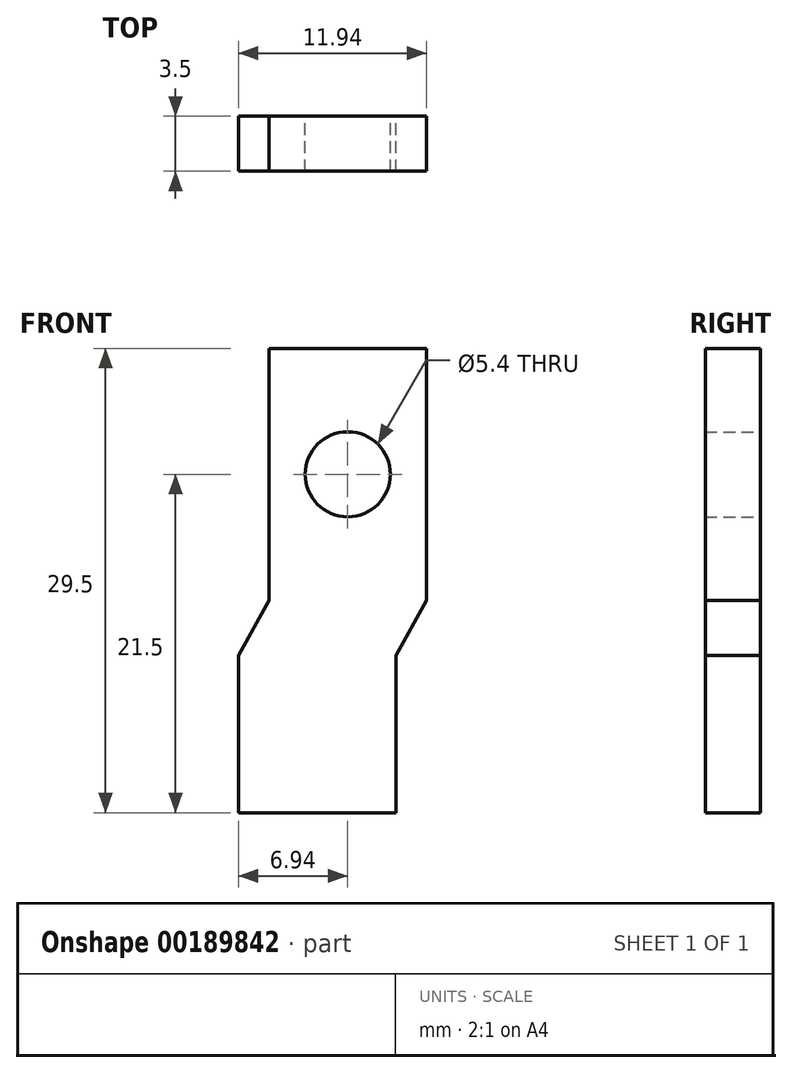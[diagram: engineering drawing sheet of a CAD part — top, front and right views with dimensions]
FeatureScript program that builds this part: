
annotation { "Feature Type Name" : "Feature", "Feature Type Description" : "" }
export const myFeature = defineFeature(function(context is Context, id is Id, definition is map)
    precondition{}
    {
        {
            var Q0;
            Q0=qCreatedBy(makeId("Front.planeOp"),FACE);
            var sketch = newSketch(context, id + "F0", { "sketchPlane" : qUnion([Q0])});
            skCircle(sketch, "E0", {"center": v(0, 0) * mm, "radius": 2.7 * mm});
            skLineSegment(sketch, "E1.bottom", {"start": v(5, 8) * mm, "end": v(-5, 8) * mm});
            skLineSegment(sketch, "E1.top", {"start": v(5, -8) * mm, "end": v(-5, -8) * mm});
            skLineSegment(sketch, "E1.left", {"start": v(5, 8) * mm, "end": v(5, -8) * mm});
            skLineSegment(sketch, "E1.right", {"start": v(-5, 8) * mm, "end": v(-5, -8) * mm});
            skLineSegment(sketch, "E2", {"start": v(-5, -8) * mm, "end": v(-6.94, -11.5) * mm});
            skLineSegment(sketch, "E3", {"start": v(-6.94, -11.5) * mm, "end": v(3.06, -11.5) * mm});
            skLineSegment(sketch, "E4", {"start": v(3.06, -11.5) * mm, "end": v(5, -8) * mm});
            skLineSegment(sketch, "E5.top", {"start": v(-6.94, -21.5) * mm, "end": v(3.06, -21.5) * mm});
            skLineSegment(sketch, "E5.left", {"start": v(-6.94, -11.5) * mm, "end": v(-6.94, -21.5) * mm});
            skLineSegment(sketch, "E5.right", {"start": v(3.06, -11.5) * mm, "end": v(3.06, -21.5) * mm});
            skSolve(sketch);
        }
        {
            var Q0;
            Q0 = qSketchRegion(id + "F0", true);
            extrude(context, id + "F1", {"entities" : qUnion([Q0]), "depth" : 3.5 * mm});
        }
    });
